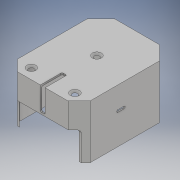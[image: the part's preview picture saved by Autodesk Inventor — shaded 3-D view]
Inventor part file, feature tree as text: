
AUTODESK INVENTOR PART (.ipt)
format: ipt  version: 2017 (Build 210142000, 142)  size: 457,728 bytes
history: native  units: mm
features: extrude x9, sketch x7, other x5, fillet x4, hole x3
ambient origin geometry x8: Origin, YZ Plane, XZ Plane, XY Plane, X Axis, Y Axis, Z Axis, Center Point
bodies: Body1 (feature_tree)
feature tree (28):
  other  "Твердое тело1"
  sketch  "Эскиз1"
  extrude  "Выдавливание1"  Depth=58.6mm
  extrude  "Выдавливание2"  Depth=77.0mm
  fillet  "Сопряжение1"  Radius=11.0mm
  extrude  "Выдавливание3"  Depth=11.0mm
  extrude  "Выдавливание4"  Depth=8.5mm
  extrude  "Выдавливание5"  Depth=8.5mm
  other  "Комбинировать1"
  hole  "Отверстие4"  [1 undecoded]
  hole  "Отверстие5"  [1 undecoded]
  hole  "Отверстие6"  [1 undecoded]
  fillet  "Сопряжение2"  Radius=11.0mm
  fillet  "Сопряжение3"  Radius=1.2mm
  extrude  "Выдавливание6"  Depth=1.5mm TaperAngle=0.0deg
  extrude  "Выдавливание7"  Depth=43.5mm TaperAngle=0.0deg
  extrude  "Выдавливание8"  Depth=1.0mm
  other  "Комбинировать2"
  fillet  "Сопряжение4"  Radius=4.0mm
  extrude  "Выдавливание10"  Depth=17.0mm
  other  "Твердое тело2"
  sketch  "Эскиз2"
  sketch  "Эскиз3"
  sketch  "Эскиз4"
  other  "Твердое тело3"
  sketch  "Эскиз5"
  sketch  "Эскиз6"
  sketch  "Эскиз8"
note: 3 required parameter values undecoded (feature->parameter linkage not recoverable at this tier; creation-order binding heuristic only, values carry confidence <= 0.55)
